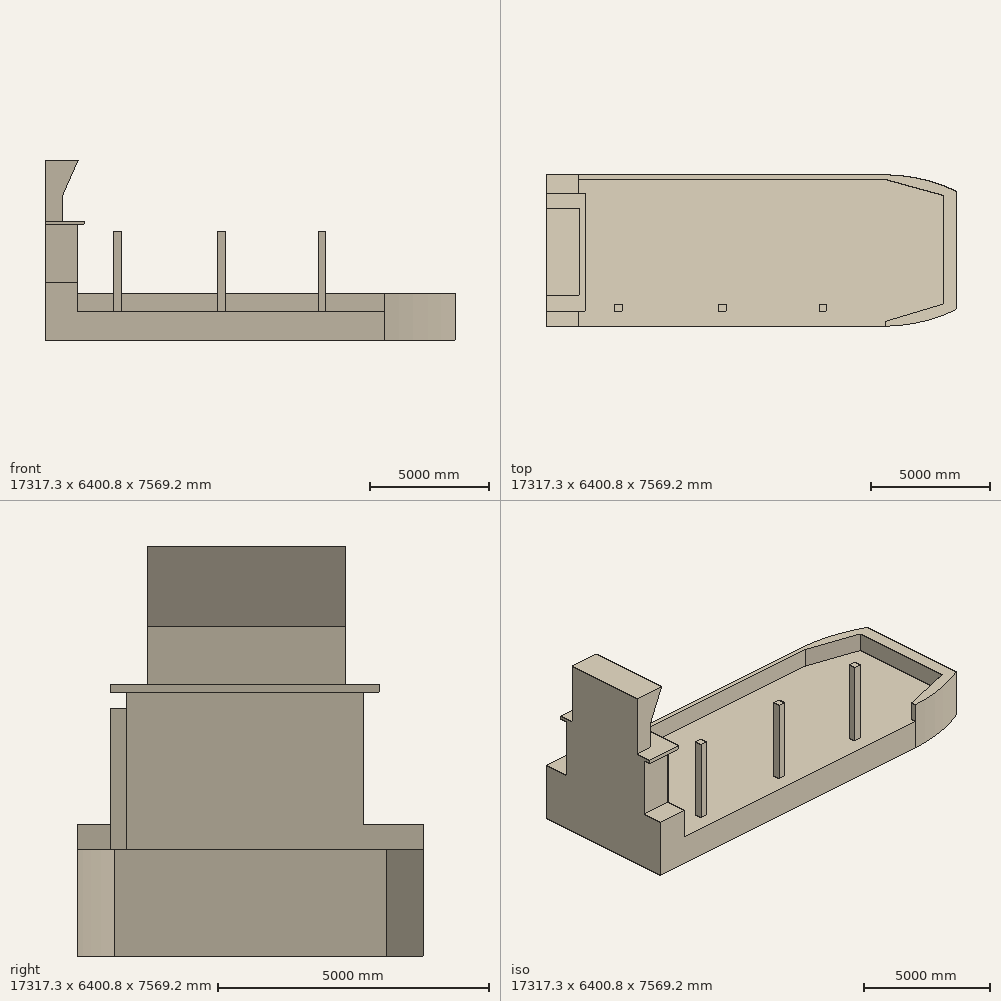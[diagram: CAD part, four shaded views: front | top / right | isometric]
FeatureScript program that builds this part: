
annotation { "Feature Type Name" : "Feature", "Feature Type Description" : "" }
export const myFeature = defineFeature(function(context is Context, id is Id, definition is map)
    precondition{}
    {
        {
            var Q0;
            Q0=qCreatedBy(makeId("Top.planeOp"),FACE);
            var sketch = newSketch(context, id + "F0", { "sketchPlane" : qUnion([Q0])});
            skLineSegment(sketch, "E0", {"start": v(11226.8, -3269.2) * mm, "end": v(-11226.8, 3269.2) * mm, "construction": true});
            skArc(sketch, "E1", {"start": v(11226.8, 2570.75) * mm, "mid": v(9766.45, 3084.79) * mm, "end": v(8229.29, 3269.2) * mm});
            skArc(sketch, "E2", {"start": v(-7983.21, 3269.2) * mm, "mid": v(-9611.3, 3167.35) * mm, "end": v(-11226.8, 2941) * mm});
            skLineSegment(sketch, "E3", {"start": v(-7983.21, 3269.2) * mm, "end": v(8229.29, 3269.2) * mm});
            skLineSegment(sketch, "E4", {"start": v(8229.29, 3269.2) * mm, "end": v(8229.29, 68.8) * mm, "construction": true});
            skLineSegment(sketch, "E5", {"start": v(11226.8, 2570.75) * mm, "end": v(11226.8, 68.8) * mm});
            skLineSegment(sketch, "E6", {"start": v(11226.8, 68.8) * mm, "end": v(-11226.8, 68.8) * mm, "construction": true});
            skLineSegment(sketch, "E7", {"start": v(-11226.8, 2941) * mm, "end": v(-11226.8, 68.8) * mm});
            skLineSegment(sketch, "E8.MirrorCS", {"start": v(11226.8, -2433.17) * mm, "end": v(11226.8, 68.8) * mm});
            skArc(sketch, "E9.MirrorCS", {"start": v(11226.8, -2433.17) * mm, "mid": v(9766.45, -2947.2) * mm, "end": v(8229.29, -3131.6) * mm});
            skLineSegment(sketch, "E10.MirrorCS", {"start": v(-7983.21, -3131.6) * mm, "end": v(8229.29, -3131.6) * mm});
            skArc(sketch, "E11.MirrorCS", {"start": v(-7983.21, -3131.6) * mm, "mid": v(-9611.3, -3029.76) * mm, "end": v(-11226.8, -2803.42) * mm});
            skLineSegment(sketch, "E12.MirrorCS", {"start": v(-11226.8, -2803.42) * mm, "end": v(-11226.8, 68.8) * mm});
            skSolve(sketch);
        }
        {
            var Q0;
            Q0 = qSketchRegion(id + "F0", true);
            extrude(context, id + "F1", {"entities" : qUnion([Q0]), "oppositeDirection" : true, "depth" : 1219.2 * mm, "offsetDistance" : 25.4 * mm});
        }
        {
            var Q0;
            Q0=makeQuery(id+"F1.opExtrude","CAP_FACE",FACE,{"disambiguationData":[OSD([sQuery(id+"F0.wireOp",EDGE,"E1"),sQuery(id+"F0.wireOp",EDGE,"E2"),sQuery(id+"F0.wireOp",EDGE,"E3"),sQuery(id+"F0.wireOp",EDGE,"E5"),sQuery(id+"F0.wireOp",EDGE,"E7"),sQuery(id+"F0.wireOp",EDGE,"E8.MirrorCS"),sQuery(id+"F0.wireOp",EDGE,"E9.MirrorCS"),sQuery(id+"F0.wireOp",EDGE,"E10.MirrorCS"),sQuery(id+"F0.wireOp",EDGE,"E11.MirrorCS"),sQuery(id+"F0.wireOp",EDGE,"E12.MirrorCS")])],"isStart":true});
            var sketch = newSketch(context, id + "F2", { "sketchPlane" : qUnion([Q0])});
            skLineSegment(sketch, "E13", {"start": v(11226.8, -3269.2) * mm, "end": v(-11226.8, 3269.2) * mm, "construction": true});
            skLineSegment(sketch, "E14.bottom", {"start": v(-4755.54, 3066) * mm, "end": v(8229.29, 3066) * mm});
            skLineSegment(sketch, "E14.top", {"start": v(-4755.54, 3269.2) * mm, "end": v(8229.29, 3269.2) * mm});
            skLineSegment(sketch, "E14.left", {"start": v(-4755.54, 3066) * mm, "end": v(-4755.54, 3269.2) * mm});
            skLineSegment(sketch, "E14.right", {"start": v(8229.29, 3066) * mm, "end": v(8229.29, 3269.2) * mm});
            skLineSegment(sketch, "E15", {"start": v(8229.29, 3066) * mm, "end": v(10662.75, 2395.75) * mm});
            skLineSegment(sketch, "E16", {"start": v(10662.75, 2395.75) * mm, "end": v(10662.75, -2201.75) * mm});
            skLineSegment(sketch, "E17", {"start": v(10662.75, -2201.75) * mm, "end": v(8229.29, -2928.4) * mm});
            skLineSegment(sketch, "E18", {"start": v(8229.29, -2928.4) * mm, "end": v(8229.29, -3131.6) * mm});
            skArc(sketch, "E19.0", {"start": v(11226.8, -2433.17) * mm, "mid": v(9766.45, -2947.2) * mm, "end": v(8229.29, -3131.6) * mm});
            skLineSegment(sketch, "E20", {"start": v(11226.8, -2433.17) * mm, "end": v(11226.8, 2570.75) * mm});
            skArc(sketch, "E21.0", {"start": v(11226.8, 2570.75) * mm, "mid": v(9766.45, 3084.79) * mm, "end": v(8229.29, 3269.2) * mm});
            skLineSegment(sketch, "E22", {"start": v(8229.29, 3269.2) * mm, "end": v(-4755.54, 3269.2) * mm});
            skSolve(sketch);
        }
        {
            var Q0;
            Q0 = qSketchRegion(id + "F2", true);
            extrude(context, id + "F3", {"entities" : qUnion([Q0]), "operationType" : NewBodyOperationType.ADD, "depth" : 762 * mm, "offsetDistance" : 25.4 * mm});
        }
        {
            var Q0;
            Q0=makeQuery(id+"F1.opExtrude","CAP_FACE",FACE,{"disambiguationData":[OSD([sQuery(id+"F0.wireOp",EDGE,"E1"),sQuery(id+"F0.wireOp",EDGE,"E2"),sQuery(id+"F0.wireOp",EDGE,"E3"),sQuery(id+"F0.wireOp",EDGE,"E5"),sQuery(id+"F0.wireOp",EDGE,"E7"),sQuery(id+"F0.wireOp",EDGE,"E8.MirrorCS"),sQuery(id+"F0.wireOp",EDGE,"E9.MirrorCS"),sQuery(id+"F0.wireOp",EDGE,"E10.MirrorCS"),sQuery(id+"F0.wireOp",EDGE,"E11.MirrorCS"),sQuery(id+"F0.wireOp",EDGE,"E12.MirrorCS")])],"isStart":true});
            var sketch = newSketch(context, id + "F4", { "sketchPlane" : qUnion([Q0])});
            skLineSegment(sketch, "E23", {"start": v(-4755.54, 3269.2) * mm, "end": v(-4755.54, -3131.6) * mm});
            skLineSegment(sketch, "E24.0", {"start": v(-7983.21, -3131.6) * mm, "end": v(-4755.54, -3131.6) * mm});
            skArc(sketch, "E24.1", {"start": v(-7983.21, -3131.6) * mm, "mid": v(-9611.3, -3029.76) * mm, "end": v(-11226.8, -2803.42) * mm});
            skLineSegment(sketch, "E24.2", {"start": v(-11226.8, 2941) * mm, "end": v(-11226.8, -2803.42) * mm});
            skArc(sketch, "E24.3", {"start": v(-7983.21, 3269.2) * mm, "mid": v(-9611.3, 3167.35) * mm, "end": v(-11226.8, 2941) * mm});
            skLineSegment(sketch, "E25.0", {"start": v(-7983.21, 3269.2) * mm, "end": v(-4755.54, 3269.2) * mm});
            skPoint(sketch, "E26.orphan", {"position": v(8229.29, -3131.6) * mm});
            skSolve(sketch);
        }
        {
            var Q0;
            Q0 = qSketchRegion(id + "F4", true);
            extrude(context, id + "F5", {"entities" : qUnion([Q0]), "operationType" : NewBodyOperationType.ADD, "depth" : 1219.2 * mm, "offsetDistance" : 25.4 * mm});
        }
        {
            var Q0;
            Q0=makeQuery(id+"F5.opExtrude","CAP_FACE",FACE,{"disambiguationData":[OSD([sQuery(id+"F4.wireOp",EDGE,"E23"),sQuery(id+"F4.wireOp",EDGE,"E24.0"),sQuery(id+"F4.wireOp",EDGE,"E24.1"),sQuery(id+"F4.wireOp",EDGE,"E24.2"),sQuery(id+"F4.wireOp",EDGE,"E24.3"),sQuery(id+"F4.wireOp",EDGE,"E25.0")])],"isStart":false});
            var sketch = newSketch(context, id + "F6", { "sketchPlane" : qUnion([Q0])});
            skLineSegment(sketch, "E27.bottom", {"start": v(-4755.54, 2151.6) * mm, "end": v(-9398, 2151.6) * mm});
            skLineSegment(sketch, "E27.top", {"start": v(-4755.54, -2217.2) * mm, "end": v(-9398, -2217.2) * mm});
            skLineSegment(sketch, "E27.left", {"start": v(-4755.54, 2151.6) * mm, "end": v(-4755.54, -2217.2) * mm});
            skLineSegment(sketch, "E27.right", {"start": v(-9398, 2151.6) * mm, "end": v(-9398, -2217.2) * mm});
            skSolve(sketch);
        }
        {
            var Q0;
            Q0 = qSketchRegion(id + "F6", true);
            extrude(context, id + "F7", {"entities" : qUnion([Q0]), "operationType" : NewBodyOperationType.ADD, "depth" : 2438.4 * mm, "offsetDistance" : 25.4 * mm});
        }
        {
            var Q0;
            Q0=makeQuery(id+"F7.opExtrude","CAP_FACE",FACE,{"disambiguationData":[OSD([sQuery(id+"F6.wireOp",EDGE,"E27.bottom"),sQuery(id+"F6.wireOp",EDGE,"E27.top"),sQuery(id+"F6.wireOp",EDGE,"E27.left"),sQuery(id+"F6.wireOp",EDGE,"E27.right")])],"isStart":false});
            var sketch = newSketch(context, id + "F8", { "sketchPlane" : qUnion([Q0])});
            skLineSegment(sketch, "E28.bottom", {"start": v(-4450.74, 2456.4) * mm, "end": v(-10160, 2456.4) * mm});
            skLineSegment(sketch, "E28.top", {"start": v(-4450.74, -2522) * mm, "end": v(-10160, -2522) * mm});
            skLineSegment(sketch, "E28.left", {"start": v(-4450.74, 2456.4) * mm, "end": v(-4450.74, -2522) * mm});
            skLineSegment(sketch, "E28.right", {"start": v(-10160, 2456.4) * mm, "end": v(-10160, -2522) * mm});
            skSolve(sketch);
        }
        {
            var Q0;
            Q0 = qSketchRegion(id + "F8", true);
            extrude(context, id + "F9", {"entities" : qUnion([Q0]), "operationType" : NewBodyOperationType.ADD, "depth" : 152.4 * mm, "offsetDistance" : 25.4 * mm});
        }
        {
            var Q0;
            Q0=qCreatedBy(makeId("Front.planeOp"),FACE);
            var sketch = newSketch(context, id + "F10", { "sketchPlane" : qUnion([Q0])});
            skLineSegment(sketch, "E29", {"start": v(-5365.14, 3810) * mm, "end": v(-5365.14, 4876.8) * mm});
            skLineSegment(sketch, "E30", {"start": v(-5365.14, 4876.8) * mm, "end": v(-4714.95, 6350) * mm});
            skLineSegment(sketch, "E31", {"start": v(-4714.95, 6350) * mm, "end": v(-9245.6, 6350) * mm});
            skLineSegment(sketch, "E32", {"start": v(-9245.6, 6350) * mm, "end": v(-9245.6, 3810) * mm});
            skLineSegment(sketch, "E33", {"start": v(-9245.6, 3810) * mm, "end": v(-5365.14, 3810) * mm});
            skSolve(sketch);
        }
        {
            var Q0;
            Q0 = qSketchRegion(id + "F10", true);
            extrude(context, id + "F11", {"entities" : qUnion([Q0]), "operationType" : NewBodyOperationType.ADD, "endBound" : BoundingType.SYMMETRIC, "depth" : 3657.6 * mm, "offsetDistance" : 25.4 * mm});
        }
        {
            var Q0;
            Q0=makeQuery(id+"F1.opExtrude","CAP_FACE",FACE,{"disambiguationData":[OSD([sQuery(id+"F0.wireOp",EDGE,"E1"),sQuery(id+"F0.wireOp",EDGE,"E2"),sQuery(id+"F0.wireOp",EDGE,"E3"),sQuery(id+"F0.wireOp",EDGE,"E5"),sQuery(id+"F0.wireOp",EDGE,"E7"),sQuery(id+"F0.wireOp",EDGE,"E8.MirrorCS"),sQuery(id+"F0.wireOp",EDGE,"E9.MirrorCS"),sQuery(id+"F0.wireOp",EDGE,"E10.MirrorCS"),sQuery(id+"F0.wireOp",EDGE,"E11.MirrorCS"),sQuery(id+"F0.wireOp",EDGE,"E12.MirrorCS")])],"isStart":true});
            var sketch = newSketch(context, id + "F12", { "sketchPlane" : qUnion([Q0])});
            skLineSegment(sketch, "E34.bottom", {"start": v(-3201.06, -2217.2) * mm, "end": v(-2896.26, -2217.2) * mm});
            skLineSegment(sketch, "E34.top", {"start": v(-3201.06, -2522) * mm, "end": v(-2896.26, -2522) * mm});
            skLineSegment(sketch, "E34.left", {"start": v(-3201.06, -2217.2) * mm, "end": v(-3201.06, -2522) * mm});
            skLineSegment(sketch, "E34.right", {"start": v(-2896.26, -2217.2) * mm, "end": v(-2896.26, -2522) * mm});
            skLineSegment(sketch, "E35.bottom", {"start": v(1191.1, -2217.2) * mm, "end": v(1495.9, -2217.2) * mm});
            skLineSegment(sketch, "E35.top", {"start": v(1191.1, -2522) * mm, "end": v(1495.9, -2522) * mm});
            skLineSegment(sketch, "E35.left", {"start": v(1191.1, -2217.2) * mm, "end": v(1191.1, -2522) * mm});
            skLineSegment(sketch, "E35.right", {"start": v(1495.9, -2217.2) * mm, "end": v(1495.9, -2522) * mm});
            skLineSegment(sketch, "E36.bottom", {"start": v(5430.87, -2217.2) * mm, "end": v(5735.67, -2217.2) * mm});
            skLineSegment(sketch, "E36.top", {"start": v(5430.87, -2522) * mm, "end": v(5735.67, -2522) * mm});
            skLineSegment(sketch, "E36.left", {"start": v(5430.87, -2217.2) * mm, "end": v(5430.87, -2522) * mm});
            skLineSegment(sketch, "E36.right", {"start": v(5735.67, -2217.2) * mm, "end": v(5735.67, -2522) * mm});
            skSolve(sketch);
        }
        {
            var Q0;
            Q0 = qSketchRegion(id + "F12", true);
            extrude(context, id + "F13", {"entities" : qUnion([Q0]), "operationType" : NewBodyOperationType.ADD, "depth" : 3352.8 * mm, "offsetDistance" : 25.4 * mm});
        }
        {
            var Q0;
            Q0=makeQuery(id+"F1.opExtrude","CAP_FACE",FACE,{"disambiguationData":[OSD([sQuery(id+"F0.wireOp",EDGE,"E1"),sQuery(id+"F0.wireOp",EDGE,"E2"),sQuery(id+"F0.wireOp",EDGE,"E3"),sQuery(id+"F0.wireOp",EDGE,"E5"),sQuery(id+"F0.wireOp",EDGE,"E7"),sQuery(id+"F0.wireOp",EDGE,"E8.MirrorCS"),sQuery(id+"F0.wireOp",EDGE,"E9.MirrorCS"),sQuery(id+"F0.wireOp",EDGE,"E10.MirrorCS"),sQuery(id+"F0.wireOp",EDGE,"E11.MirrorCS"),sQuery(id+"F0.wireOp",EDGE,"E12.MirrorCS")])],"isStart":false});
            var sketch = newSketch(context, id + "F14", { "sketchPlane" : qUnion([Q0])});
            skLineSegment(sketch, "E37.bottom", {"start": v(-6090.54, 3717.2) * mm, "end": v(-11890.3, 3717.2) * mm});
            skLineSegment(sketch, "E37.top", {"start": v(-6090.54, -4660.24) * mm, "end": v(-11890.3, -4660.24) * mm});
            skLineSegment(sketch, "E37.left", {"start": v(-6090.54, 3717.2) * mm, "end": v(-6090.54, -4660.24) * mm});
            skLineSegment(sketch, "E37.right", {"start": v(-11890.3, 3717.2) * mm, "end": v(-11890.3, -4660.24) * mm});
            skSolve(sketch);
        }
        {
            var Q0;
            Q0 = qSketchRegion(id + "F14", true);
            extrude(context, id + "F15", {"entities" : qUnion([Q0]), "operationType" : NewBodyOperationType.REMOVE, "endBound" : BoundingType.THROUGH_ALL, "oppositeDirection" : true, "depth" : 25.4 * mm, "offsetDistance" : 25.4 * mm});
        }
    });
